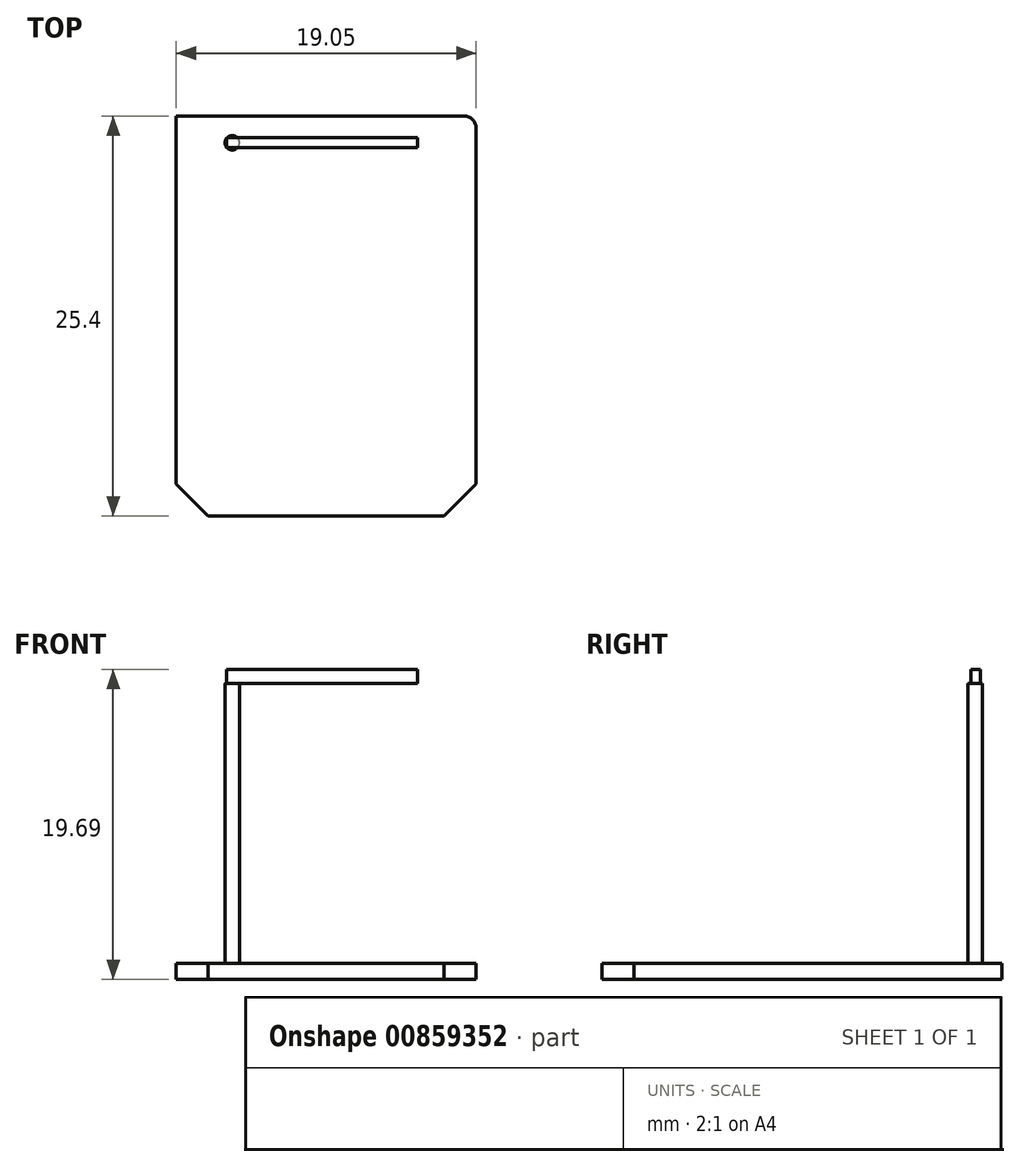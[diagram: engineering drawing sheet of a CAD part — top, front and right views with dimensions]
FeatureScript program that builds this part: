
annotation { "Feature Type Name" : "Feature", "Feature Type Description" : "" }
export const myFeature = defineFeature(function(context is Context, id is Id, definition is map)
    precondition{}
    {
        {
            var Q0;
            Q0=qCreatedBy(makeId("Top.planeOp"),FACE);
            var sketch = newSketch(context, id + "F0", { "sketchPlane" : qUnion([Q0])});
            skLineSegment(sketch, "E0.bottom", {"start": v(0, 0) * mm, "end": v(19.05, 0) * mm});
            skLineSegment(sketch, "E0.top", {"start": v(0, 25.4) * mm, "end": v(19.05, 25.4) * mm});
            skLineSegment(sketch, "E0.left", {"start": v(0, 0) * mm, "end": v(0, 25.4) * mm});
            skLineSegment(sketch, "E0.right", {"start": v(19.05, 0) * mm, "end": v(19.05, 25.4) * mm});
            skSolve(sketch);
        }
        {
            var Q0;
            Q0=makeQuery(id+"F0.imprint","IMPRINT",FACE,{"disambiguationData":[TD([[makeQuery(id+"F0.imprint","IMPRINT",EDGE,{"derivedFrom":sQuery(id+"F0.wireOp",EDGE,"E0.bottom")}),1.0]])]});
            extrude(context, id + "F1", {"entities" : qUnion([Q0]), "depth" : 1.02 * mm, "offsetDistance" : 25.4 * mm});
        }
        {
            var Q0;
            Q0=makeQuery(id+"F1.opExtrude","SWEPT_EDGE",EDGE,{"disambiguationData":[OSD([sQuery(id+"F0.wireOp",EDGE,"E0.bottom"),sQuery(id+"F0.wireOp",EDGE,"E0.left")])]});
            chamfer(context, id + "F2", {"entities" : qUnion([Q0]), "width" : 2.03 * mm, "tangentPropagation" : true});
        }
        {
            var Q0;
            Q0=makeQuery(id+"F1.opExtrude","SWEPT_EDGE",EDGE,{"disambiguationData":[OSD([sQuery(id+"F0.wireOp",EDGE,"E0.bottom"),sQuery(id+"F0.wireOp",EDGE,"E0.right")])]});
            chamfer(context, id + "F3", {"entities" : qUnion([Q0]), "width" : 2.03 * mm, "tangentPropagation" : true});
        }
        {
            var Q0;
            Q0=makeQuery(id+"F1.opExtrude","SWEPT_EDGE",EDGE,{"disambiguationData":[OSD([sQuery(id+"F0.wireOp",EDGE,"E0.top"),sQuery(id+"F0.wireOp",EDGE,"E0.right")])]});
            fillet(context, id + "F4", {"entities" : qUnion([Q0]), "radius" : 0.76 * mm, "tangentPropagation" : true, "allowEdgeOverflow" : false});
        }
        {
            var Q0;
            Q0=makeQuery(id+"F1.opExtrude","CAP_FACE",FACE,{"disambiguationData":[OSD([sQuery(id+"F0.wireOp",EDGE,"E0.bottom"),sQuery(id+"F0.wireOp",EDGE,"E0.top"),sQuery(id+"F0.wireOp",EDGE,"E0.left"),sQuery(id+"F0.wireOp",EDGE,"E0.right")])],"isStart":false});
            var sketch = newSketch(context, id + "F5", { "sketchPlane" : qUnion([Q0])});
            skLineSegment(sketch, "E1.bottom", {"start": v(0.89, 22) * mm, "end": v(18, 22) * mm});
            skLineSegment(sketch, "E1.top", {"start": v(0.89, 25.4) * mm, "end": v(18, 25.4) * mm});
            skCircle(sketch, "E2", {"center": v(3.56, 23.7) * mm, "radius": 0.46 * mm});
            skCircle(sketch, "E3", {"center": v(14.98, 23.7) * mm, "radius": 0.46 * mm});
            skSolve(sketch);
        }
        {
            var Q0;
            Q0=makeQuery(id+"F5.imprint","IMPRINT",FACE,{"disambiguationData":[TD([[makeQuery(id+"F5.imprint","IMPRINT",EDGE,{"derivedFrom":sQuery(id+"F5.wireOp",EDGE,"E2")}),1.0]])]});
            extrude(context, id + "F6", {"entities" : qUnion([Q0]), "operationType" : NewBodyOperationType.ADD, "depth" : 17.78 * mm, "offsetDistance" : 25.4 * mm});
        }
        {
            var Q0;
            Q0=sQuery(id+"F5.wireOp",EDGE,"E3");
            extrude(context, id + "F7", {"bodyType" : ToolBodyType.SURFACE, "surfaceEntities" : qUnion([Q0]), "depth" : 17.78 * mm, "offsetDistance" : 25.4 * mm});
        }
        {
            var Q0;
            Q0=makeQuery(id+"F6.opExtrude","CAP_FACE",FACE,{"disambiguationData":[OSD([sQuery(id+"F5.wireOp",EDGE,"E2")])],"isStart":false});
            var sketch = newSketch(context, id + "F8", { "sketchPlane" : qUnion([Q0])});
            skLineSegment(sketch, "E4.bottom", {"start": v(3.2, 23.4) * mm, "end": v(15.34, 23.4) * mm});
            skLineSegment(sketch, "E4.top", {"start": v(3.2, 24.02) * mm, "end": v(15.34, 24.02) * mm});
            skLineSegment(sketch, "E4.left", {"start": v(3.2, 23.4) * mm, "end": v(3.2, 24.02) * mm});
            skLineSegment(sketch, "E4.right", {"start": v(15.34, 23.4) * mm, "end": v(15.34, 24.02) * mm});
            skSolve(sketch);
        }
        {
            var Q0;
            {var subQ0=sQuery(id+"F8.wireOp",EDGE,"E4.right");Q0=makeQuery(id+"F8.imprint","IMPRINT",FACE,{"disambiguationData":[TD([[makeQuery(id+"F8.imprint","IMPRINT",EDGE,{"derivedFrom":subQ0}),1.0]])]});}
            var Q1;
            {var subQ1=makeQuery(id+"F6.opExtrude","CAP_EDGE",EDGE,{"disambiguationData":[OSD([sQuery(id+"F5.wireOp",EDGE,"E2")])],"isStart":false});var subQ3=sQuery(id+"F8.wireOp",EDGE,"E4.top");var subQ7=makeQuery(id+"F8.imprint","INTERSECT",VERTEX,{"disambiguationData":[OD(0.0)],"derivedFrom":[subQ1,subQ3]});Q1=makeQuery(id+"F8.imprint","IMPRINT",FACE,{"disambiguationData":[TD([[makeQuery(id+"F8.imprint","IMPRINT",EDGE,{"disambiguationData":[TD([[subQ7,-1.0]])],"derivedFrom":subQ3}),-1.0]])]});}
            extrude(context, id + "F9", {"entities" : qUnion([Q0, Q1]), "operationType" : NewBodyOperationType.ADD, "depth" : 0.89 * mm, "offsetDistance" : 25.4 * mm});
        }
    });
